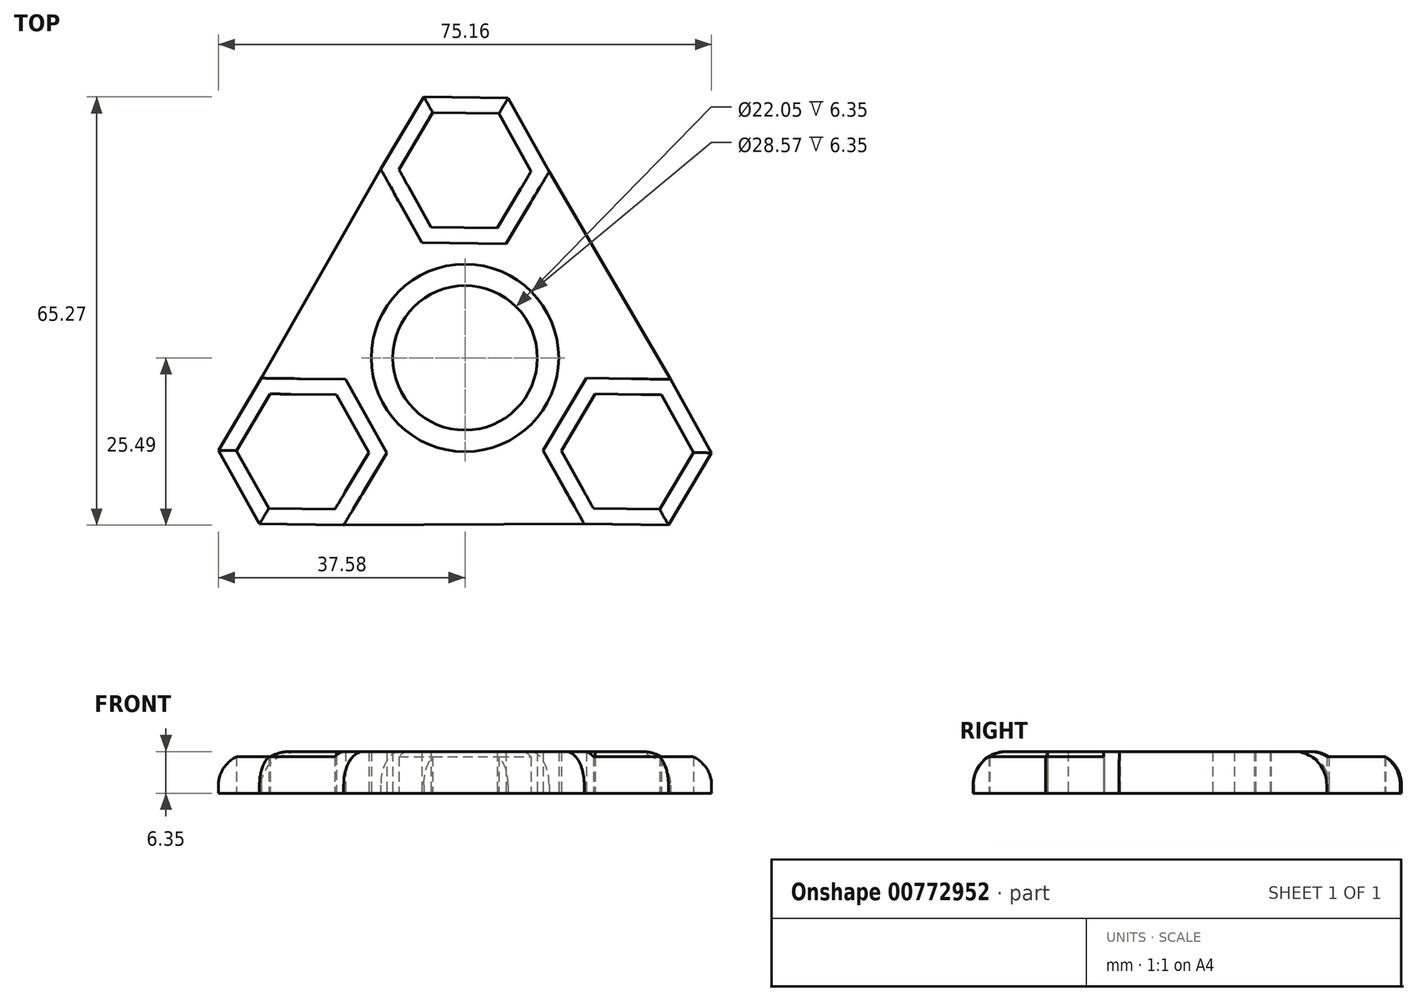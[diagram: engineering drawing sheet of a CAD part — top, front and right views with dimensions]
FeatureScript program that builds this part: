
annotation { "Feature Type Name" : "Feature", "Feature Type Description" : "" }
export const myFeature = defineFeature(function(context is Context, id is Id, definition is map)
    precondition{}
    {
        {
            var Q0;
            Q0=qCreatedBy(makeId("Top.planeOp"),FACE);
            var sketch = newSketch(context, id + "F0", { "sketchPlane" : qUnion([Q0])});
            skCircle(sketch, "E0", {"center": v(0, 0) * mm, "radius": 14.29 * mm});
            skCircle(sketch, "E1", {"center": v(0, 0) * mm, "radius": 11.02 * mm});
            skCircle(sketch, "E2.cCircle", {"center": v(0, 28.58) * mm, "radius": 8.73 * mm, "construction": true});
            skLineSegment(sketch, "E2.0", {"start": v(10.08, 28.43) * mm, "end": v(4.92, 19.77) * mm});
            skLineSegment(sketch, "E2.1", {"start": v(4.92, 19.77) * mm, "end": v(-5.16, 19.92) * mm});
            skLineSegment(sketch, "E2.2", {"start": v(-5.16, 19.92) * mm, "end": v(-10.08, 28.72) * mm});
            skLineSegment(sketch, "E2.3", {"start": v(-10.08, 28.72) * mm, "end": v(-4.92, 37.38) * mm});
            skLineSegment(sketch, "E2.4", {"start": v(-4.92, 37.38) * mm, "end": v(5.16, 37.23) * mm});
            skLineSegment(sketch, "E2.5", {"start": v(5.16, 37.23) * mm, "end": v(10.08, 28.43) * mm});
            skPoint(sketch, "E2.0.midPoint", {"position": v(7.5, 24.1) * mm});
            skCircle(sketch, "E3.cCircle", {"center": v(0, 28.58) * mm, "radius": 11.11 * mm, "construction": true});
            skLineSegment(sketch, "E3.0", {"start": v(12.83, 28.4) * mm, "end": v(6.26, 17.37) * mm});
            skLineSegment(sketch, "E3.1", {"start": v(6.26, 17.37) * mm, "end": v(-6.57, 17.55) * mm});
            skLineSegment(sketch, "E3.2", {"start": v(-6.57, 17.55) * mm, "end": v(-12.83, 28.76) * mm});
            skLineSegment(sketch, "E3.3", {"start": v(-12.83, 28.76) * mm, "end": v(-6.26, 39.78) * mm});
            skLineSegment(sketch, "E3.4", {"start": v(-6.26, 39.78) * mm, "end": v(6.57, 39.6) * mm});
            skLineSegment(sketch, "E3.5", {"start": v(6.57, 39.6) * mm, "end": v(12.83, 28.4) * mm});
            skPoint(sketch, "E3.0.midPoint", {"position": v(9.54, 22.88) * mm});
            skPoint(sketch, "E4.1.0", {"position": v(-24.59, -3.18) * mm});
            skCircle(sketch, "E4.1.1", {"center": v(-24.75, -14.29) * mm, "radius": 8.73 * mm, "construction": true});
            skLineSegment(sketch, "E4.1.2", {"start": v(-19.58, -5.63) * mm, "end": v(-14.67, -14.43) * mm});
            skLineSegment(sketch, "E4.1.3", {"start": v(-34.83, -14.14) * mm, "end": v(-29.66, -5.49) * mm});
            skCircle(sketch, "E4.1.4", {"center": v(-24.75, -14.29) * mm, "radius": 11.11 * mm, "construction": true});
            skLineSegment(sketch, "E4.1.5", {"start": v(-18.17, -3.27) * mm, "end": v(-11.92, -14.47) * mm});
            skPoint(sketch, "E4.1.6", {"position": v(-24.62, -5.56) * mm});
            skLineSegment(sketch, "E4.1.7", {"start": v(-18.49, -25.5) * mm, "end": v(-31.32, -25.3) * mm});
            skLineSegment(sketch, "E4.1.8", {"start": v(-31.32, -25.3) * mm, "end": v(-37.58, -14.1) * mm});
            skLineSegment(sketch, "E4.1.9", {"start": v(-37.58, -14.1) * mm, "end": v(-31, -3.08) * mm});
            skLineSegment(sketch, "E4.1.10", {"start": v(-29.66, -5.49) * mm, "end": v(-19.58, -5.63) * mm});
            skLineSegment(sketch, "E4.1.11", {"start": v(-14.67, -14.43) * mm, "end": v(-19.83, -23.09) * mm});
            skLineSegment(sketch, "E4.1.12", {"start": v(-19.83, -23.09) * mm, "end": v(-29.91, -22.95) * mm});
            skLineSegment(sketch, "E4.1.13", {"start": v(-29.91, -22.95) * mm, "end": v(-34.83, -14.14) * mm});
            skLineSegment(sketch, "E4.1.14", {"start": v(-31, -3.08) * mm, "end": v(-18.17, -3.27) * mm});
            skLineSegment(sketch, "E4.1.15", {"start": v(-11.92, -14.47) * mm, "end": v(-18.49, -25.5) * mm});
            skPoint(sketch, "E4.2.0", {"position": v(15.04, -19.7) * mm});
            skCircle(sketch, "E4.2.1", {"center": v(24.75, -14.29) * mm, "radius": 8.73 * mm, "construction": true});
            skLineSegment(sketch, "E4.2.2", {"start": v(14.67, -14.14) * mm, "end": v(19.83, -5.49) * mm});
            skLineSegment(sketch, "E4.2.3", {"start": v(29.66, -23.09) * mm, "end": v(19.58, -22.95) * mm});
            skCircle(sketch, "E4.2.4", {"center": v(24.75, -14.29) * mm, "radius": 11.11 * mm, "construction": true});
            skLineSegment(sketch, "E4.2.5", {"start": v(11.92, -14.1) * mm, "end": v(18.49, -3.08) * mm});
            skPoint(sketch, "E4.2.6", {"position": v(17.12, -18.55) * mm});
            skLineSegment(sketch, "E4.2.7", {"start": v(31.32, -3.27) * mm, "end": v(37.58, -14.47) * mm});
            skLineSegment(sketch, "E4.2.8", {"start": v(37.58, -14.47) * mm, "end": v(31, -25.5) * mm});
            skLineSegment(sketch, "E4.2.9", {"start": v(31, -25.5) * mm, "end": v(18.17, -25.3) * mm});
            skLineSegment(sketch, "E4.2.10", {"start": v(19.58, -22.95) * mm, "end": v(14.67, -14.14) * mm});
            skLineSegment(sketch, "E4.2.11", {"start": v(19.83, -5.49) * mm, "end": v(29.91, -5.63) * mm});
            skLineSegment(sketch, "E4.2.12", {"start": v(29.91, -5.63) * mm, "end": v(34.83, -14.43) * mm});
            skLineSegment(sketch, "E4.2.13", {"start": v(34.83, -14.43) * mm, "end": v(29.66, -23.09) * mm});
            skLineSegment(sketch, "E4.2.14", {"start": v(18.17, -25.3) * mm, "end": v(11.92, -14.1) * mm});
            skLineSegment(sketch, "E4.2.15", {"start": v(18.49, -3.08) * mm, "end": v(31.32, -3.27) * mm});
            skSolve(sketch);
        }
        {
            var Q0;
            Q0=qCreatedBy(makeId("Top.planeOp"),FACE);
            var sketch = newSketch(context, id + "F1", { "sketchPlane" : qUnion([Q0])});
            skCircle(sketch, "E5.0", {"center": v(0, 28.58) * mm, "radius": 11.11 * mm});
            skLineSegment(sketch, "E5.1", {"start": v(5.16, 37.23) * mm, "end": v(10.08, 28.43) * mm});
            skLineSegment(sketch, "E5.2", {"start": v(-4.92, 37.38) * mm, "end": v(5.16, 37.23) * mm});
            skLineSegment(sketch, "E5.3", {"start": v(11.92, -14.1) * mm, "end": v(18.49, -3.08) * mm});
            skLineSegment(sketch, "E5.4", {"start": v(-34.83, -14.14) * mm, "end": v(-29.66, -5.49) * mm});
            skLineSegment(sketch, "E5.5", {"start": v(-10.08, 28.72) * mm, "end": v(-4.92, 37.38) * mm});
            skLineSegment(sketch, "E5.6", {"start": v(19.58, -22.95) * mm, "end": v(14.67, -14.14) * mm});
            skLineSegment(sketch, "E5.7", {"start": v(-5.16, 19.92) * mm, "end": v(-10.08, 28.72) * mm});
            skLineSegment(sketch, "E5.8", {"start": v(4.92, 19.77) * mm, "end": v(-5.16, 19.92) * mm});
            skLineSegment(sketch, "E5.9", {"start": v(10.08, 28.43) * mm, "end": v(4.92, 19.77) * mm});
            skLineSegment(sketch, "E5.10", {"start": v(-31.32, -25.3) * mm, "end": v(-37.58, -14.1) * mm});
            skLineSegment(sketch, "E5.11", {"start": v(14.67, -14.14) * mm, "end": v(19.83, -5.49) * mm});
            skLineSegment(sketch, "E5.12", {"start": v(-14.67, -14.43) * mm, "end": v(-19.83, -23.09) * mm});
            skLineSegment(sketch, "E5.13", {"start": v(34.83, -14.43) * mm, "end": v(29.66, -23.09) * mm});
            skCircle(sketch, "E5.14", {"center": v(0, 28.58) * mm, "radius": 8.73 * mm});
            skCircle(sketch, "E5.15", {"center": v(0, 0) * mm, "radius": 11.02 * mm});
            skCircle(sketch, "E5.16", {"center": v(0, 0) * mm, "radius": 14.29 * mm});
            skLineSegment(sketch, "E5.17", {"start": v(6.57, 39.6) * mm, "end": v(12.83, 28.4) * mm});
            skCircle(sketch, "E5.18", {"center": v(24.75, -14.29) * mm, "radius": 11.11 * mm});
            skLineSegment(sketch, "E5.19", {"start": v(-19.58, -5.63) * mm, "end": v(-14.67, -14.43) * mm});
            skLineSegment(sketch, "E5.20", {"start": v(31, -25.5) * mm, "end": v(18.17, -25.3) * mm});
            skCircle(sketch, "E5.21", {"center": v(24.75, -14.29) * mm, "radius": 8.73 * mm});
            skLineSegment(sketch, "E5.22", {"start": v(-6.26, 39.78) * mm, "end": v(6.57, 39.6) * mm});
            skLineSegment(sketch, "E5.23", {"start": v(-12.83, 28.76) * mm, "end": v(-6.26, 39.78) * mm});
            skLineSegment(sketch, "E5.24", {"start": v(-18.49, -25.5) * mm, "end": v(-31.32, -25.3) * mm});
            skLineSegment(sketch, "E5.25", {"start": v(31.32, -3.27) * mm, "end": v(37.58, -14.47) * mm});
            skLineSegment(sketch, "E5.26", {"start": v(-29.66, -5.49) * mm, "end": v(-19.58, -5.63) * mm});
            skLineSegment(sketch, "E5.27", {"start": v(-31, -3.08) * mm, "end": v(-18.17, -3.27) * mm});
            skLineSegment(sketch, "E5.28", {"start": v(29.91, -5.63) * mm, "end": v(34.83, -14.43) * mm});
            skLineSegment(sketch, "E5.29", {"start": v(29.66, -23.09) * mm, "end": v(19.58, -22.95) * mm});
            skCircle(sketch, "E5.30", {"center": v(-24.75, -14.29) * mm, "radius": 8.73 * mm});
            skLineSegment(sketch, "E5.31", {"start": v(-11.92, -14.47) * mm, "end": v(-18.49, -25.5) * mm});
            skLineSegment(sketch, "E5.32", {"start": v(37.58, -14.47) * mm, "end": v(31, -25.5) * mm});
            skLineSegment(sketch, "E5.33", {"start": v(-18.17, -3.27) * mm, "end": v(-11.92, -14.47) * mm});
            skCircle(sketch, "E5.34", {"center": v(-24.75, -14.29) * mm, "radius": 11.11 * mm});
            skLineSegment(sketch, "E5.35", {"start": v(-19.83, -23.09) * mm, "end": v(-29.91, -22.95) * mm});
            skLineSegment(sketch, "E5.36", {"start": v(19.83, -5.49) * mm, "end": v(29.91, -5.63) * mm});
            skLineSegment(sketch, "E5.37", {"start": v(-37.58, -14.1) * mm, "end": v(-31, -3.08) * mm});
            skLineSegment(sketch, "E5.38", {"start": v(-29.91, -22.95) * mm, "end": v(-34.83, -14.14) * mm});
            skLineSegment(sketch, "E5.39", {"start": v(18.49, -3.08) * mm, "end": v(31.32, -3.27) * mm});
            skLineSegment(sketch, "E5.40", {"start": v(-6.57, 17.55) * mm, "end": v(-12.83, 28.76) * mm});
            skLineSegment(sketch, "E5.41", {"start": v(18.17, -25.3) * mm, "end": v(11.92, -14.1) * mm});
            skLineSegment(sketch, "E5.42", {"start": v(6.26, 17.37) * mm, "end": v(-6.57, 17.55) * mm});
            skLineSegment(sketch, "E5.43", {"start": v(12.83, 28.4) * mm, "end": v(6.26, 17.37) * mm});
            skLineSegment(sketch, "E6", {"start": v(-12.83, 28.76) * mm, "end": v(-31, -3.08) * mm});
            skLineSegment(sketch, "E7", {"start": v(-18.49, -25.5) * mm, "end": v(18.17, -25.3) * mm});
            skLineSegment(sketch, "E8", {"start": v(31.32, -3.27) * mm, "end": v(12.83, 28.4) * mm});
            skSolve(sketch);
        }
        {
            var Q0;
            Q0=makeQuery(id+"F1.imprint","IMPRINT",FACE,{"disambiguationData":[TD([[makeQuery(id+"F1.imprint","IMPRINT",EDGE,{"derivedFrom":sQuery(id+"F1.wireOp",EDGE,"E5.16")}),-1.0]])]});
            var Q1;
            Q1=makeQuery(id+"F0.imprint","IMPRINT",FACE,{"disambiguationData":[TD([[makeQuery(id+"F0.imprint","IMPRINT",EDGE,{"derivedFrom":sQuery(id+"F0.wireOp",EDGE,"E2.0")}),1.0]])]});
            var Q2;
            Q2=makeQuery(id+"F0.imprint","IMPRINT",FACE,{"disambiguationData":[TD([[makeQuery(id+"F0.imprint","IMPRINT",EDGE,{"derivedFrom":sQuery(id+"F0.wireOp",EDGE,"E0")}),1.0]])]});
            var Q3;
            Q3=makeQuery(id+"F0.imprint","IMPRINT",FACE,{"disambiguationData":[TD([[makeQuery(id+"F0.imprint","IMPRINT",EDGE,{"derivedFrom":sQuery(id+"F0.wireOp",EDGE,"E4.2.2")}),1.0]])]});
            var Q4;
            Q4=makeQuery(id+"F0.imprint","IMPRINT",FACE,{"disambiguationData":[TD([[makeQuery(id+"F0.imprint","IMPRINT",EDGE,{"derivedFrom":sQuery(id+"F0.wireOp",EDGE,"E4.1.2")}),1.0]])]});
            extrude(context, id + "F2", {"entities" : qUnion([Q0, Q1, Q2, Q3, Q4]), "depth" : 6.35 * mm, "offsetDistance" : 25.4 * mm});
        }
        {
            var Q0;
            Q0=makeQuery(id+"F2.opExtrude","CAP_EDGE",EDGE,{"disambiguationData":[OSD([sQuery(id+"F0.wireOp",EDGE,"E3.3")])],"isStart":false});
            var Q1;
            Q1=makeQuery(id+"F2.opExtrude","CAP_EDGE",EDGE,{"disambiguationData":[OSD([sQuery(id+"F1.wireOp",EDGE,"E6")])],"isStart":false});
            var Q2;
            Q2=makeQuery(id+"F2.opExtrude","CAP_EDGE",EDGE,{"disambiguationData":[OSD([sQuery(id+"F0.wireOp",EDGE,"E4.1.9")])],"isStart":false});
            var Q3;
            Q3=makeQuery(id+"F2.opExtrude","CAP_EDGE",EDGE,{"disambiguationData":[OSD([sQuery(id+"F0.wireOp",EDGE,"E4.1.8")])],"isStart":false});
            var Q4;
            Q4=makeQuery(id+"F2.opExtrude","CAP_EDGE",EDGE,{"disambiguationData":[OSD([sQuery(id+"F0.wireOp",EDGE,"E4.1.7")])],"isStart":false});
            var Q5;
            Q5=makeQuery(id+"F2.opExtrude","CAP_EDGE",EDGE,{"disambiguationData":[OSD([sQuery(id+"F1.wireOp",EDGE,"E7")])],"isStart":false});
            var Q6;
            Q6=makeQuery(id+"F2.opExtrude","CAP_EDGE",EDGE,{"disambiguationData":[OSD([sQuery(id+"F0.wireOp",EDGE,"E4.2.9")])],"isStart":false});
            var Q7;
            Q7=makeQuery(id+"F2.opExtrude","CAP_EDGE",EDGE,{"disambiguationData":[OSD([sQuery(id+"F0.wireOp",EDGE,"E4.2.8")])],"isStart":false});
            var Q8;
            Q8=makeQuery(id+"F2.opExtrude","CAP_EDGE",EDGE,{"disambiguationData":[OSD([sQuery(id+"F0.wireOp",EDGE,"E4.2.7")])],"isStart":false});
            var Q9;
            Q9=makeQuery(id+"F2.opExtrude","CAP_EDGE",EDGE,{"disambiguationData":[OSD([sQuery(id+"F1.wireOp",EDGE,"E8")])],"isStart":false});
            var Q10;
            Q10=makeQuery(id+"F2.opExtrude","CAP_EDGE",EDGE,{"disambiguationData":[OSD([sQuery(id+"F0.wireOp",EDGE,"E3.5")])],"isStart":false});
            var Q11;
            Q11=makeQuery(id+"F2.opExtrude","CAP_EDGE",EDGE,{"disambiguationData":[OSD([sQuery(id+"F0.wireOp",EDGE,"E3.4")])],"isStart":false});
            fillet(context, id + "F3", {"entities" : qUnion([Q0, Q1, Q2, Q3, Q4, Q5, Q6, Q7, Q8, Q9, Q10, Q11]), "radius" : 5.08 * mm, "tangentPropagation" : true, "allowEdgeOverflow" : false});
        }
    });
